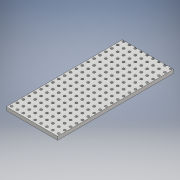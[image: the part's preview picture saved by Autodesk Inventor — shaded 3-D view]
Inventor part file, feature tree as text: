
AUTODESK INVENTOR PART (.ipt)
format: ipt  version: 2017.3 (Build 213257000, 257)  size: 334,848 bytes
history: native  units: mm
features: sketch x3, extrude x2, hole x1
ambient origin geometry x8: Origin, YZ Plane, XZ Plane, XY Plane, X Axis, Y Axis, Z Axis, Center Point
bodies: Volumenkörper1 (feature_tree)
feature tree (6):
  extrude  "Extrusion1"  Depth=50.0mm
  hole  "Bohrung1"  [1 undecoded]
  extrude  "Extrusion2"  Depth=120.0mm
  sketch  "Skizze1"  dims[d0=30.0mm d1=50.0mm]
  sketch  "Skizze2"  dims[d2=1.5mm d3=0.0mm d4=1.27mm]
  sketch  "Skizze3"  dims[d5=1.27mm d6=120.0mm d8=2.54mm d9=200.0mm d11=2.54mm d14=1.0mm d15=6.0mm d16=4.0mm d17=2.0mm d18=90.0deg d19=8.0mm d20=0.0mm d21=7.9mm d22=0.0mm]
note: 1 required parameter value undecoded (feature->parameter linkage not recoverable at this tier; creation-order binding heuristic only, values carry confidence <= 0.55)
